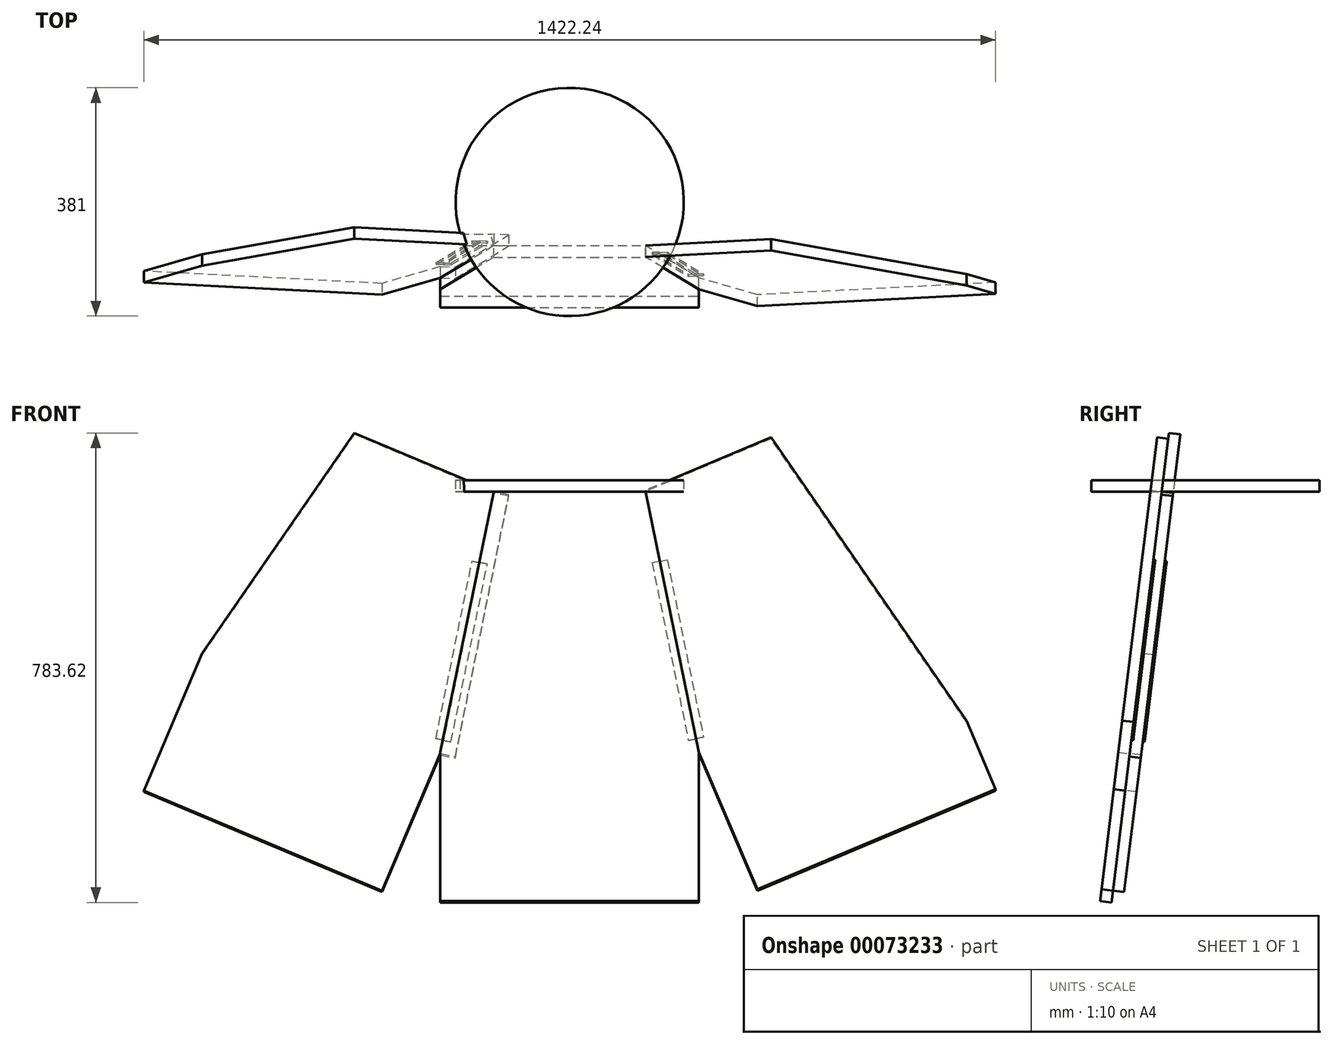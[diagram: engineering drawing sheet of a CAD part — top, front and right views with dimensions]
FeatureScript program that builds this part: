
annotation { "Feature Type Name" : "Feature", "Feature Type Description" : "" }
export const myFeature = defineFeature(function(context is Context, id is Id, definition is map)
    precondition{}
    {
        {
            var Q0;
            Q0=qCreatedBy(makeId("Top.planeOp"),FACE);
            var sketch = newSketch(context, id + "F0", { "sketchPlane" : qUnion([Q0])});
            skCircle(sketch, "E0", {"center": v(0, 0) * mm, "radius": 190.5 * mm});
            skLineSegment(sketch, "E1", {"start": v(164.98, -95.25) * mm, "end": v(0, 190.5) * mm, "construction": true});
            skLineSegment(sketch, "E2", {"start": v(164.98, -95.25) * mm, "end": v(-164.98, -95.25) * mm, "construction": true});
            skLineSegment(sketch, "E3", {"start": v(-164.98, -95.25) * mm, "end": v(0, 190.5) * mm, "construction": true});
            skSolve(sketch);
        }
        {
            var Q0;
            Q0=qCreatedBy(makeId("Top.planeOp"),FACE);
            var sketch = newSketch(context, id + "F1", { "sketchPlane" : qUnion([Q0])});
            skLineSegment(sketch, "E4.0", {"start": v(-126.48, -73.03) * mm, "end": v(0, 146.05) * mm, "construction": true});
            skLineSegment(sketch, "E4.1", {"start": v(126.48, -73.03) * mm, "end": v(-126.48, -73.03) * mm, "construction": true});
            skLineSegment(sketch, "E4.2", {"start": v(126.48, -73.03) * mm, "end": v(0, 146.05) * mm, "construction": true});
            skLineSegment(sketch, "E5.0", {"start": v(266.7, -153.98) * mm, "end": v(0, 307.96) * mm, "construction": true});
            skLineSegment(sketch, "E5.1", {"start": v(266.7, -153.98) * mm, "end": v(-266.7, -153.98) * mm, "construction": true});
            skLineSegment(sketch, "E5.2", {"start": v(-266.7, -153.98) * mm, "end": v(0, 307.96) * mm, "construction": true});
            skCircle(sketch, "E6", {"center": v(0, 0) * mm, "radius": 307.96 * mm, "construction": true});
            skSolve(sketch);
        }
        {
            var Q0;
            Q0=makeQuery(id+"F0.imprint","IMPRINT",FACE,{"disambiguationData":[TD([[makeQuery(id+"F0.imprint","IMPRINT",EDGE,{"derivedFrom":sQuery(id+"F0.wireOp",EDGE,"E0")}),1.0]])]});
            extrude(context, id + "F2", {"entities" : qUnion([Q0]), "depth" : 19.05 * mm});
        }
        {
            var Q0;
            Q0=sQuery(id+"F1.wireOp",EDGE,"E4.1");
            cPlane(context, id + "F3", {"entities" : qUnion([Q0]), "cplaneType" : CPlaneType.LINE_ANGLE, "offset" : 152.4 * mm, "angle" : 7 * degree, "width" : 152.4 * mm, "height" : 152.4 * mm});
        }
        {
            var Q0;
            Q0=qCreatedBy(id+"F3.planeOp",FACE);
            var sketch = newSketch(context, id + "F4", { "sketchPlane" : qUnion([Q0])});
            skLineSegment(sketch, "E7.0", {"start": v(126.48, -8.9) * mm, "end": v(-126.48, -8.9) * mm, "construction": true});
            skLineSegment(sketch, "E8", {"start": v(-126.48, -8.9) * mm, "end": v(126.48, -8.9) * mm});
            skLineSegment(sketch, "E9", {"start": v(-126.48, -8.9) * mm, "end": v(-266.7, -699.78) * mm, "construction": true});
            skLineSegment(sketch, "E10", {"start": v(-266.7, -699.78) * mm, "end": v(266.7, -699.78) * mm, "construction": true});
            skLineSegment(sketch, "E11", {"start": v(266.7, -699.78) * mm, "end": v(126.48, -8.9) * mm, "construction": true});
            skLineSegment(sketch, "E12", {"start": v(-126.48, -8.9) * mm, "end": v(-215.9, -449.48) * mm});
            skLineSegment(sketch, "E13", {"start": v(-215.9, -449.48) * mm, "end": v(-215.9, -699.78) * mm});
            skLineSegment(sketch, "E14", {"start": v(-215.9, -699.78) * mm, "end": v(215.9, -699.78) * mm});
            skLineSegment(sketch, "E15", {"start": v(215.9, -699.78) * mm, "end": v(215.9, -449.48) * mm});
            skLineSegment(sketch, "E16", {"start": v(215.9, -449.48) * mm, "end": v(126.48, -8.9) * mm});
            skLineSegment(sketch, "E17.MirrorCS", {"start": v(-126.48, -8.9) * mm, "end": v(-359.43, 89.72) * mm});
            skLineSegment(sketch, "E18.MirrorCS", {"start": v(-613.54, -281.14) * mm, "end": v(-359.43, 89.72) * mm});
            skLineSegment(sketch, "E19.MirrorCS", {"start": v(-711.12, -511.64) * mm, "end": v(-613.54, -281.14) * mm});
            skLineSegment(sketch, "E20.MirrorCS", {"start": v(-313.48, -679.98) * mm, "end": v(-711.12, -511.64) * mm});
            skLineSegment(sketch, "E21.MirrorCS", {"start": v(-215.9, -449.48) * mm, "end": v(-313.48, -679.98) * mm});
            skLineSegment(sketch, "E22.MirrorCS", {"start": v(336.04, 79.82) * mm, "end": v(126.48, -8.9) * mm});
            skLineSegment(sketch, "E23.MirrorCS", {"start": v(359.43, 89.72) * mm, "end": v(613.54, -281.14) * mm, "construction": true});
            skLineSegment(sketch, "E24.MirrorCS", {"start": v(662.33, -396.39) * mm, "end": v(711.12, -511.64) * mm});
            skLineSegment(sketch, "E25.MirrorCS", {"start": v(711.12, -511.64) * mm, "end": v(313.48, -679.98) * mm});
            skLineSegment(sketch, "E26.MirrorCS", {"start": v(313.48, -679.98) * mm, "end": v(215.9, -449.48) * mm});
            skLineSegment(sketch, "E27", {"start": v(662.33, -396.39) * mm, "end": v(336.04, 79.82) * mm});
            skPoint(sketch, "E28.orphan", {"position": v(613.54, -281.14) * mm});
            skPoint(sketch, "E29.orphan", {"position": v(359.43, 89.72) * mm});
            skSolve(sketch);
        }
        {
            var Q0;
            Q0=makeQuery(id+"F4.imprint","IMPRINT",FACE,{"disambiguationData":[TD([[makeQuery(id+"F4.imprint","IMPRINT",EDGE,{"derivedFrom":sQuery(id+"F4.wireOp",EDGE,"E8")}),-1.0]])]});
            extrude(context, id + "F5", {"entities" : qUnion([Q0]), "depth" : 19.05 * mm});
        }
        {
            var Q0;
            Q0=makeQuery(id+"F4.imprint","IMPRINT",FACE,{"disambiguationData":[TD([[makeQuery(id+"F4.imprint","IMPRINT",EDGE,{"derivedFrom":sQuery(id+"F4.wireOp",EDGE,"E16")}),-1.0]])]});
            extrude(context, id + "F6", {"entities" : qUnion([Q0]), "depth" : 19.05 * mm});
        }
        {
            var Q0;
            Q0=makeQuery(id+"F4.imprint","IMPRINT",FACE,{"disambiguationData":[TD([[makeQuery(id+"F4.imprint","IMPRINT",EDGE,{"derivedFrom":sQuery(id+"F4.wireOp",EDGE,"E12")}),-1.0]])]});
            extrude(context, id + "F7", {"entities" : qUnion([Q0]), "oppositeDirection" : true, "depth" : 19.05 * mm});
        }
        {
            var Q0;
            Q0=makeQuery(id+"F4.imprint","IMPRINT",FACE,{"disambiguationData":[TD([[makeQuery(id+"F4.imprint","IMPRINT",EDGE,{"derivedFrom":sQuery(id+"F4.wireOp",EDGE,"E8")}),-1.0]])]});
            var sketch = newSketch(context, id + "F8", { "sketchPlane" : qUnion([Q0])});
            skLineSegment(sketch, "E30.0", {"start": v(-126.48, -8.9) * mm, "end": v(-215.9, -449.48) * mm});
            skLineSegment(sketch, "E31", {"start": v(-215.9, -449.48) * mm, "end": v(-191, -454.53) * mm});
            skLineSegment(sketch, "E32", {"start": v(-191, -454.53) * mm, "end": v(-101.6, -13.95) * mm});
            skLineSegment(sketch, "E33", {"start": v(-101.6, -13.95) * mm, "end": v(-126.48, -8.9) * mm});
            skSolve(sketch);
        }
        {
            var Q0;
            Q0=makeQuery(id+"F8.imprint","IMPRINT",FACE,{"disambiguationData":[TD([[makeQuery(id+"F8.imprint","IMPRINT",EDGE,{"derivedFrom":sQuery(id+"F8.wireOp",EDGE,"E30.0")}),1.0]])]});
            extrude(context, id + "F9", {"entities" : qUnion([Q0]), "operationType" : NewBodyOperationType.ADD, "oppositeDirection" : true, "depth" : 19.05 * mm});
        }
        {
            var Q0;
            Q0=makeQuery(id+"F9.opExtrude","CAP_FACE",FACE,{"disambiguationData":[OSD([sQuery(id+"F8.wireOp",EDGE,"E30.0"),sQuery(id+"F8.wireOp",EDGE,"E31"),sQuery(id+"F8.wireOp",EDGE,"E32"),sQuery(id+"F8.wireOp",EDGE,"E33")])],"isStart":false});
            var sketch = newSketch(context, id + "F10", { "sketchPlane" : qUnion([Q0])});
            skLineSegment(sketch, "E34", {"start": v(210.85, -424.58) * mm, "end": v(198.2, -427.15) * mm});
            skLineSegment(sketch, "E35", {"start": v(198.2, -427.15) * mm, "end": v(137.58, -128.44) * mm});
            skLineSegment(sketch, "E36", {"start": v(137.58, -128.44) * mm, "end": v(150.22, -125.87) * mm});
            skLineSegment(sketch, "E37", {"start": v(150.22, -125.87) * mm, "end": v(210.85, -424.58) * mm});
            skSolve(sketch);
        }
        {
            var Q0;
            Q0=makeQuery(id+"F10.imprint","IMPRINT",FACE,{"disambiguationData":[TD([[makeQuery(id+"F10.imprint","IMPRINT",EDGE,{"derivedFrom":sQuery(id+"F10.wireOp",EDGE,"E34")}),-1.0]])]});
            extrude(context, id + "F11", {"entities" : qUnion([Q0]), "depth" : 3.17 * mm});
        }
        {
            var Q0;
            Q0=makeQuery(id+"F11.opExtrude","SWEPT_BODY",BODY,{"disambiguationData":[OSD([sQuery(id+"F10.wireOp",EDGE,"E34"),sQuery(id+"F10.wireOp",EDGE,"E35"),sQuery(id+"F10.wireOp",EDGE,"E36"),sQuery(id+"F10.wireOp",EDGE,"E37")])]});
            var Q1;
            Q1=makeQuery(id+"F11.opExtrude","SWEPT_FACE",FACE,{"disambiguationData":[OSD([sQuery(id+"F10.wireOp",EDGE,"E37")])]});
            mirror(context, id + "F12", {"entities" : qUnion([Q0]), "mirrorPlane" : qUnion([Q1])});
        }
        {
            var Q0;
            Q0=makeQuery(id+"F4.imprint","IMPRINT",FACE,{"disambiguationData":[TD([[makeQuery(id+"F4.imprint","IMPRINT",EDGE,{"derivedFrom":sQuery(id+"F4.wireOp",EDGE,"E16")}),-1.0]])]});
            var sketch = newSketch(context, id + "F13", { "sketchPlane" : qUnion([Q0])});
            skLineSegment(sketch, "E38", {"start": v(223.5, -422.02) * mm, "end": v(210.85, -424.58) * mm});
            skLineSegment(sketch, "E39", {"start": v(210.85, -424.58) * mm, "end": v(150.22, -125.87) * mm});
            skLineSegment(sketch, "E40", {"start": v(150.22, -125.87) * mm, "end": v(162.87, -123.3) * mm});
            skLineSegment(sketch, "E41", {"start": v(162.87, -123.3) * mm, "end": v(223.5, -422.02) * mm});
            skSolve(sketch);
        }
        {
            var Q0;
            Q0 = qSketchRegion(id + "F13", true);
            extrude(context, id + "F14", {"entities" : qUnion([Q0]), "oppositeDirection" : true, "depth" : 3.17 * mm});
        }
        {
            var Q0;
            Q0=makeQuery(id+"F14.opExtrude","SWEPT_BODY",BODY,{"disambiguationData":[OSD([sQuery(id+"F13.wireOp",EDGE,"E38"),sQuery(id+"F13.wireOp",EDGE,"E39"),sQuery(id+"F13.wireOp",EDGE,"E40"),sQuery(id+"F13.wireOp",EDGE,"E41")])]});
            var Q1;
            Q1=makeQuery(id+"F14.opExtrude","SWEPT_FACE",FACE,{"disambiguationData":[OSD([sQuery(id+"F13.wireOp",EDGE,"E39")])]});
            mirror(context, id + "F15", {"entities" : qUnion([Q0]), "mirrorPlane" : qUnion([Q1])});
        }
    });
